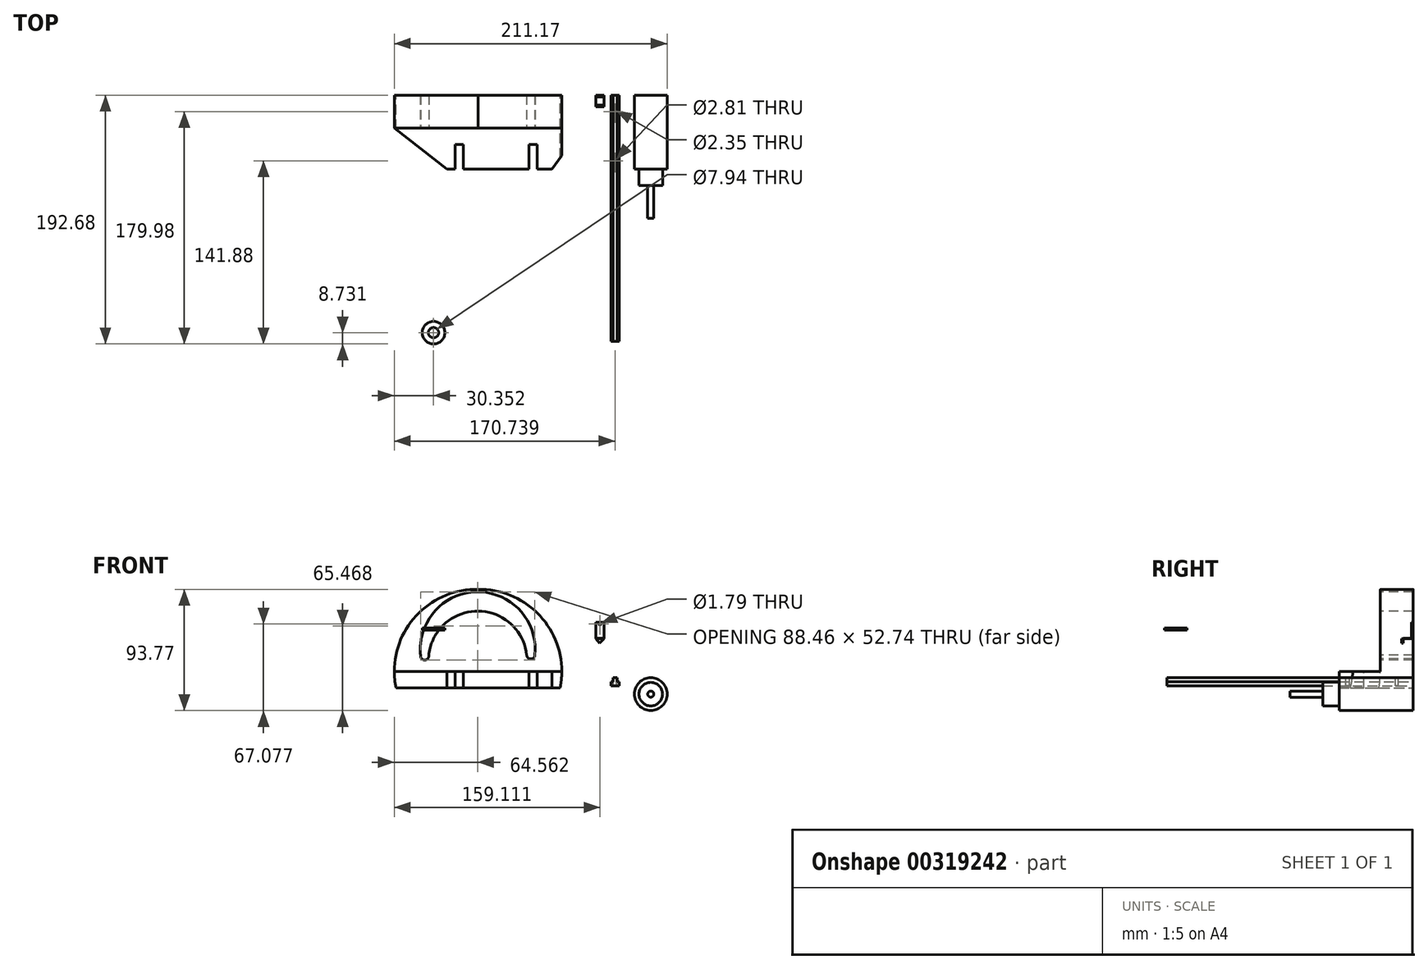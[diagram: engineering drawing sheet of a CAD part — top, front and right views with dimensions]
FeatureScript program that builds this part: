
annotation { "Feature Type Name" : "Feature", "Feature Type Description" : "" }
export const myFeature = defineFeature(function(context is Context, id is Id, definition is map)
    precondition{}
    {
        {
            var Q0;
            Q0=qCreatedBy(makeId("Front.planeOp"),FACE);
            var sketch = newSketch(context, id + "F0", { "sketchPlane" : qUnion([Q0])});
            skLineSegment(sketch, "E0", {"start": v(-59.8, -44.8) * mm, "end": v(67.2, -44.8) * mm});
            skLineSegment(sketch, "E1", {"start": v(-59.8, -44.8) * mm, "end": v(3.7, -44.8) * mm});
            skLineSegment(sketch, "E2", {"start": v(3.7, -44.8) * mm, "end": v(3.7, 31.4) * mm});
            skArc(sketch, "E3", {"start": v(67.2, -44.8) * mm, "mid": v(53.77, 8.57) * mm, "end": v(3.7, 31.4) * mm});
            skArc(sketch, "E4", {"start": v(3.7, 31.4) * mm, "mid": v(-46.37, 8.57) * mm, "end": v(-59.8, -44.8) * mm});
            skSolve(sketch);
        }
        {
            var Q0;
            Q0=makeQuery(id+"F0.imprint","IMPRINT",FACE,{"disambiguationData":[TD([[makeQuery(id+"F0.imprint","IMPRINT",EDGE,{"derivedFrom":sQuery(id+"F0.wireOp",EDGE,"E1")}),1.0]])]});
            var Q1;
            Q1=makeQuery(id+"F0.imprint","IMPRINT",FACE,{"disambiguationData":[TD([[makeQuery(id+"F0.imprint","IMPRINT",EDGE,{"derivedFrom":sQuery(id+"F0.wireOp",EDGE,"E0")}),1.0]])]});
            extrude(context, id + "F1", {"entities" : qUnion([Q0, Q1]), "depth" : 25.4 * mm});
        }
        {
            var Q0;
            Q0=makeQuery(id+"F1.opExtrude","CAP_FACE",FACE,{"disambiguationData":[OSD([sQuery(id+"F0.wireOp",EDGE,"E0"),sQuery(id+"F0.wireOp",EDGE,"E1"),sQuery(id+"F0.wireOp",EDGE,"E3"),sQuery(id+"F0.wireOp",EDGE,"E4")])],"isStart":false});
            var sketch = newSketch(context, id + "F2", { "sketchPlane" : qUnion([Q0])});
            skLineSegment(sketch, "E5", {"start": v(3.7, -44.8) * mm, "end": v(3.7, -32.1) * mm});
            skLineSegment(sketch, "E6", {"start": v(3.7, -32.1) * mm, "end": v(68.48, -32.1) * mm});
            skLineSegment(sketch, "E7", {"start": v(68.48, -32.1) * mm, "end": v(-61.09, -32.1) * mm});
            skSolve(sketch);
        }
        {
            var Q0;
            Q0 = qSketchRegion(id + "F2", true);
            var Q1;
            {var subQ0=sQuery(id+"F2.wireOp",EDGE,"E5");Q1=makeQuery(id+"F2.imprint","IMPRINT",FACE,{"disambiguationData":[TD([[makeQuery(id+"F2.imprint","IMPRINT",EDGE,{"derivedFrom":subQ0}),-1.0]])]});}
            var Q2;
            {var subQ0=sQuery(id+"F2.wireOp",EDGE,"E5");Q2=makeQuery(id+"F2.imprint","IMPRINT",FACE,{"disambiguationData":[TD([[makeQuery(id+"F2.imprint","IMPRINT",EDGE,{"derivedFrom":subQ0}),1.0]])]});}
            extrude(context, id + "F3", {"entities" : qUnion([Q0, Q1, Q2]), "operationType" : NewBodyOperationType.ADD, "depth" : 31.75 * mm});
        }
        {
            var Q0;
            Q0=makeQuery(id+"F3.opExtrude","SWEPT_FACE",FACE,{"disambiguationData":[OSD([sQuery(id+"F2.wireOp",EDGE,"E7")])]});
            var sketch = newSketch(context, id + "F4", { "sketchPlane" : qUnion([Q0])});
            skLineSegment(sketch, "E8", {"start": v(68.48, -57.15) * mm, "end": v(-20.42, -57.15) * mm});
            skLineSegment(sketch, "E9", {"start": v(-20.42, -57.15) * mm, "end": v(-61.09, -25.4) * mm});
            skLineSegment(sketch, "E10", {"start": v(-20.42, -57.15) * mm, "end": v(-14.07, -57.15) * mm});
            skLineSegment(sketch, "E11", {"start": v(-14.07, -57.15) * mm, "end": v(-14.07, -38.1) * mm});
            skLineSegment(sketch, "E12", {"start": v(-14.07, -38.1) * mm, "end": v(-7.72, -38.1) * mm});
            skLineSegment(sketch, "E13", {"start": v(-7.72, -38.1) * mm, "end": v(-7.72, -57.15) * mm});
            skLineSegment(sketch, "E14", {"start": v(-7.72, -57.15) * mm, "end": v(43.08, -57.15) * mm});
            skLineSegment(sketch, "E15", {"start": v(43.08, -57.15) * mm, "end": v(43.08, -38.1) * mm});
            skLineSegment(sketch, "E16", {"start": v(43.08, -38.1) * mm, "end": v(49.43, -38.1) * mm});
            skLineSegment(sketch, "E17", {"start": v(49.43, -38.1) * mm, "end": v(49.43, -57.15) * mm});
            skSolve(sketch);
        }
        {
            var Q0;
            {var subQ0=sQuery(id+"F4.wireOp",EDGE,"E11");Q0=makeQuery(id+"F4.imprint","IMPRINT",FACE,{"disambiguationData":[TD([[makeQuery(id+"F4.imprint","IMPRINT",EDGE,{"derivedFrom":subQ0}),-1.0]])]});}
            var Q1;
            {var subQ0=sQuery(id+"F4.wireOp",EDGE,"E15");Q1=makeQuery(id+"F4.imprint","IMPRINT",FACE,{"disambiguationData":[TD([[makeQuery(id+"F4.imprint","IMPRINT",EDGE,{"derivedFrom":subQ0}),-1.0]])]});}
            extrude(context, id + "F5", {"entities" : qUnion([Q0, Q1]), "operationType" : NewBodyOperationType.REMOVE, "oppositeDirection" : true, "depth" : 25.4 * mm});
        }
        {
            var Q0;
            Q0=makeQuery(id+"F3.opExtrude","SWEPT_FACE",FACE,{"disambiguationData":[OSD([sQuery(id+"F2.wireOp",EDGE,"E7")])]});
            var sketch = newSketch(context, id + "F6", { "sketchPlane" : qUnion([Q0])});
            skLineSegment(sketch, "E18", {"start": v(-14.07, -57.15) * mm, "end": v(-20.42, -57.15) * mm});
            skLineSegment(sketch, "E19", {"start": v(-20.42, -57.15) * mm, "end": v(-61.09, -25.48) * mm});
            skSolve(sketch);
        }
        {
            var Q0;
            Q0 = qSketchRegion(id + "F6", true);
            var Q1;
            {var subQ0=sQuery(id+"F6.wireOp",EDGE,"E19");Q1=makeQuery(id+"F6.imprint","IMPRINT",FACE,{"disambiguationData":[TD([[makeQuery(id+"F6.imprint","IMPRINT",EDGE,{"derivedFrom":subQ0}),1.0]])]});}
            extrude(context, id + "F7", {"entities" : qUnion([Q0, Q1]), "operationType" : NewBodyOperationType.REMOVE, "oppositeDirection" : true, "depth" : 25.4 * mm});
        }
        {
            var Q0;
            Q0=qCreatedBy(makeId("Front.planeOp"),FACE);
            var sketch = newSketch(context, id + "F8", { "sketchPlane" : qUnion([Q0])});
            skLineSegment(sketch, "E20", {"start": v(106.47, -43.18) * mm, "end": v(112.82, -43.18) * mm});
            skLineSegment(sketch, "E21", {"start": v(112.82, -43.18) * mm, "end": v(112.82, -40) * mm});
            skLineSegment(sketch, "E22", {"start": v(112.82, -40) * mm, "end": v(111.24, -40) * mm});
            skLineSegment(sketch, "E23", {"start": v(111.24, -40) * mm, "end": v(111.24, -36.83) * mm});
            skLineSegment(sketch, "E24", {"start": v(106.47, -43.18) * mm, "end": v(106.47, -40) * mm});
            skLineSegment(sketch, "E25", {"start": v(106.47, -40) * mm, "end": v(108.06, -40) * mm});
            skLineSegment(sketch, "E26", {"start": v(108.06, -40) * mm, "end": v(108.06, -36.83) * mm});
            skLineSegment(sketch, "E27", {"start": v(108.06, -36.83) * mm, "end": v(111.24, -36.83) * mm});
            skSolve(sketch);
        }
        {
            var Q0;
            Q0 = qSketchRegion(id + "F8", true);
            var Q1;
            Q1=makeQuery(id+"F8.imprint","IMPRINT",FACE,{"disambiguationData":[TD([[makeQuery(id+"F8.imprint","IMPRINT",EDGE,{"derivedFrom":sQuery(id+"F8.wireOp",EDGE,"E20")}),1.0]])]});
            extrude(context, id + "F9", {"entities" : qUnion([Q0, Q1]), "depth" : 190.5 * mm});
        }
        {
            var Q0;
            Q0=makeQuery(id+"F1.opExtrude","CAP_FACE",FACE,{"disambiguationData":[OSD([sQuery(id+"F0.wireOp",EDGE,"E0"),sQuery(id+"F0.wireOp",EDGE,"E1"),sQuery(id+"F0.wireOp",EDGE,"E3"),sQuery(id+"F0.wireOp",EDGE,"E4")])],"isStart":false});
            var sketch = newSketch(context, id + "F10", { "sketchPlane" : qUnion([Q0])});
            skArc(sketch, "E28", {"start": v(41.35, -19.4) * mm, "mid": v(3.47, 14.6) * mm, "end": v(-34.4, -19.4) * mm});
            skArc(sketch, "E29", {"start": v(47.7, -19.4) * mm, "mid": v(3.47, 29.5) * mm, "end": v(-40.76, -19.4) * mm});
            skPoint(sketch, "E30.end.orphan", {"position": v(-34.4, -32.1) * mm});
            skPoint(sketch, "E31.end.orphan", {"position": v(41.35, -32.1) * mm});
            skArc(sketch, "E32", {"start": v(-40.76, -19.4) * mm, "mid": v(-37.58, -23.25) * mm, "end": v(-34.4, -19.4) * mm});
            skArc(sketch, "E33", {"start": v(41.35, -19.4) * mm, "mid": v(44.53, -22.45) * mm, "end": v(47.7, -19.4) * mm});
            skSolve(sketch);
        }
        {
            var Q0;
            Q0=makeQuery(id+"F10.imprint","IMPRINT",FACE,{"disambiguationData":[TD([[makeQuery(id+"F10.imprint","IMPRINT",EDGE,{"derivedFrom":sQuery(id+"F10.wireOp",EDGE,"E28")}),-1.0]])]});
            extrude(context, id + "F11", {"entities" : qUnion([Q0]), "operationType" : NewBodyOperationType.REMOVE, "oppositeDirection" : true, "depth" : 25.4 * mm});
        }
        {
            var Q0;
            Q0=makeQuery(id+"F3.opExtrude","SWEPT_FACE",FACE,{"disambiguationData":[OSD([sQuery(id+"F2.wireOp",EDGE,"E7")])]});
            var sketch = newSketch(context, id + "F12", { "sketchPlane" : qUnion([Q0])});
            skLineSegment(sketch, "E34", {"start": v(61, -57.15) * mm, "end": v(68.48, -46.88) * mm});
            skSolve(sketch);
        }
        {
            var Q0;
            Q0 = qSketchRegion(id + "F12", true);
            var Q1;
            {var subQ0=sQuery(id+"F12.wireOp",EDGE,"E34");Q1=makeQuery(id+"F12.imprint","IMPRINT",FACE,{"disambiguationData":[TD([[makeQuery(id+"F12.imprint","IMPRINT",EDGE,{"derivedFrom":subQ0}),-1.0]])]});}
            extrude(context, id + "F13", {"entities" : qUnion([Q0, Q1]), "operationType" : NewBodyOperationType.REMOVE, "oppositeDirection" : true, "depth" : 25.4 * mm});
        }
        {
            var Q0;
            Q0=qCreatedBy(makeId("Front.planeOp"),FACE);
            var sketch = newSketch(context, id + "F14", { "sketchPlane" : qUnion([Q0])});
            skCircle(sketch, "E35", {"center": v(137.38, -49.65) * mm, "radius": 12.7 * mm});
            skSolve(sketch);
        }
        {
            var Q0;
            Q0 = qSketchRegion(id + "F14", true);
            var Q1;
            Q1=makeQuery(id+"F14.imprint","IMPRINT",FACE,{"disambiguationData":[TD([[makeQuery(id+"F14.imprint","IMPRINT",EDGE,{"derivedFrom":sQuery(id+"F14.wireOp",EDGE,"E35")}),1.0]])]});
            extrude(context, id + "F15", {"entities" : qUnion([Q0, Q1]), "depth" : 57.15 * mm});
        }
        {
            var Q0;
            Q0=makeQuery(id+"F15.opExtrude","CAP_FACE",FACE,{"disambiguationData":[OSD([sQuery(id+"F14.wireOp",EDGE,"E35")])],"isStart":false});
            var sketch = newSketch(context, id + "F16", { "sketchPlane" : qUnion([Q0])});
            skCircle(sketch, "E36", {"center": v(137.38, -49.65) * mm, "radius": 9.13 * mm});
            skSolve(sketch);
        }
        {
            var Q0;
            Q0=makeQuery(id+"F16.imprint","IMPRINT",FACE,{"disambiguationData":[TD([[makeQuery(id+"F16.imprint","IMPRINT",EDGE,{"derivedFrom":sQuery(id+"F16.wireOp",EDGE,"E36")}),1.0]])]});
            extrude(context, id + "F17", {"entities" : qUnion([Q0]), "operationType" : NewBodyOperationType.ADD, "depth" : 12.7 * mm});
        }
        {
            var Q0;
            Q0=makeQuery(id+"F17.opExtrude","CAP_FACE",FACE,{"disambiguationData":[OSD([sQuery(id+"F16.wireOp",EDGE,"E36")])],"isStart":false});
            var sketch = newSketch(context, id + "F18", { "sketchPlane" : qUnion([Q0])});
            skCircle(sketch, "E37", {"center": v(137.38, -49.65) * mm, "radius": 2.38 * mm});
            skSolve(sketch);
        }
        {
            var Q0;
            Q0=makeQuery(id+"F18.imprint","IMPRINT",FACE,{"disambiguationData":[TD([[makeQuery(id+"F18.imprint","IMPRINT",EDGE,{"derivedFrom":sQuery(id+"F18.wireOp",EDGE,"E37")}),1.0]])]});
            extrude(context, id + "F19", {"entities" : qUnion([Q0]), "operationType" : NewBodyOperationType.ADD, "depth" : 25.4 * mm});
        }
        {
            var Q0;
            Q0=makeQuery(id+"F9.opExtrude","SWEPT_FACE",FACE,{"disambiguationData":[OSD([sQuery(id+"F8.wireOp",EDGE,"E27")])]});
            var sketch = newSketch(context, id + "F20", { "sketchPlane" : qUnion([Q0])});
            skLineSegment(sketch, "E38", {"start": v(109.65, -190.5) * mm, "end": v(109.65, -50.8) * mm});
            skCircle(sketch, "E39", {"center": v(109.65, -50.8) * mm, "radius": 1.4 * mm});
            skSolve(sketch);
        }
        {
            var Q0;
            Q0=makeQuery(id+"F20.imprint","IMPRINT",FACE,{"disambiguationData":[TD([[makeQuery(id+"F20.imprint","IMPRINT",EDGE,{"derivedFrom":sQuery(id+"F20.wireOp",EDGE,"E39")}),1.0]])]});
            extrude(context, id + "F21", {"entities" : qUnion([Q0]), "operationType" : NewBodyOperationType.REMOVE, "oppositeDirection" : true, "depth" : 25.4 * mm});
        }
        {
            var Q0;
            Q0=qCreatedBy(makeId("Top.planeOp"),FACE);
            var sketch = newSketch(context, id + "F22", { "sketchPlane" : qUnion([Q0])});
            skCircle(sketch, "E40", {"center": v(-30.74, -183.95) * mm, "radius": 8.73 * mm});
            skCircle(sketch, "E41", {"center": v(-30.74, -183.95) * mm, "radius": 3.97 * mm});
            skSolve(sketch);
        }
        {
            var Q0;
            Q0=makeQuery(id+"F22.imprint","IMPRINT",FACE,{"disambiguationData":[TD([[makeQuery(id+"F22.imprint","IMPRINT",EDGE,{"derivedFrom":sQuery(id+"F22.wireOp",EDGE,"E40")}),1.0]])]});
            extrude(context, id + "F23", {"entities" : qUnion([Q0]), "depth" : 1.59 * mm});
        }
        {
            var Q0;
            Q0=qCreatedBy(makeId("Front.planeOp"),FACE);
            var sketch = newSketch(context, id + "F24", { "sketchPlane" : qUnion([Q0])});
            skLineSegment(sketch, "E42", {"start": v(94.85, 6) * mm, "end": v(94.85, -6.7) * mm});
            skLineSegment(sketch, "E43", {"start": v(94.85, -6.7) * mm, "end": v(101.2, -6.7) * mm});
            skLineSegment(sketch, "E44", {"start": v(101.2, -6.7) * mm, "end": v(101.2, 6) * mm});
            skLineSegment(sketch, "E45", {"start": v(101.2, 6) * mm, "end": v(94.85, 6) * mm});
            skSolve(sketch);
        }
        {
            var Q0;
            Q0 = qSketchRegion(id + "F24", true);
            var Q1;
            Q1=makeQuery(id+"F24.imprint","IMPRINT",FACE,{"disambiguationData":[TD([[makeQuery(id+"F24.imprint","IMPRINT",EDGE,{"derivedFrom":sQuery(id+"F24.wireOp",EDGE,"E42")}),1.0]])]});
            extrude(context, id + "F25", {"entities" : qUnion([Q0, Q1]), "depth" : 1.41 * mm});
        }
        {
            var Q0;
            Q0=makeQuery(id+"F25.opExtrude","CAP_FACE",FACE,{"disambiguationData":[OSD([sQuery(id+"F24.wireOp",EDGE,"E42"),sQuery(id+"F24.wireOp",EDGE,"E43"),sQuery(id+"F24.wireOp",EDGE,"E44"),sQuery(id+"F24.wireOp",EDGE,"E45")])],"isStart":false});
            var sketch = newSketch(context, id + "F26", { "sketchPlane" : qUnion([Q0])});
            skLineSegment(sketch, "E46", {"start": v(94.85, -6.37) * mm, "end": v(101.2, -6.37) * mm});
            skLineSegment(sketch, "E47", {"start": v(101.2, -6.37) * mm, "end": v(101.2, -6.7) * mm});
            skLineSegment(sketch, "E48", {"start": v(101.2, -6.7) * mm, "end": v(94.85, -6.7) * mm});
            skLineSegment(sketch, "E49", {"start": v(94.85, -6.7) * mm, "end": v(94.85, -6.37) * mm});
            skSolve(sketch);
        }
        {
            var Q0;
            Q0=makeQuery(id+"F26.imprint","IMPRINT",FACE,{"disambiguationData":[TD([[makeQuery(id+"F26.imprint","IMPRINT",EDGE,{"derivedFrom":sQuery(id+"F26.wireOp",EDGE,"E46")}),-1.0]])]});
            extrude(context, id + "F27", {"entities" : qUnion([Q0]), "operationType" : NewBodyOperationType.ADD, "depth" : 6.35 * mm});
        }
        {
            var Q0;
            Q0=makeQuery(id+"F27.opExtrude","CAP_FACE",FACE,{"disambiguationData":[OSD([sQuery(id+"F26.wireOp",EDGE,"E46"),sQuery(id+"F26.wireOp",EDGE,"E47"),sQuery(id+"F26.wireOp",EDGE,"E48"),sQuery(id+"F26.wireOp",EDGE,"E49")])],"isStart":false});
            var sketch = newSketch(context, id + "F28", { "sketchPlane" : qUnion([Q0])});
            skLineSegment(sketch, "E50", {"start": v(94.85, -6.7) * mm, "end": v(97.84, -10.12) * mm});
            skLineSegment(sketch, "E51", {"start": v(97.84, -10.12) * mm, "end": v(101.2, -6.7) * mm});
            skSolve(sketch);
        }
        {
            var Q0;
            Q0 = qSketchRegion(id + "F28", true);
            var Q1;
            Q1=makeQuery(id+"F28.imprint","IMPRINT",FACE,{"disambiguationData":[TD([[makeQuery(id+"F28.imprint","IMPRINT",EDGE,{"derivedFrom":sQuery(id+"F28.wireOp",EDGE,"E50")}),1.0]])]});
            extrude(context, id + "F29", {"entities" : qUnion([Q0, Q1]), "depth" : 1.41 * mm});
        }
        {
            var Q0;
            Q0=makeQuery(id+"F25.opExtrude","CAP_FACE",FACE,{"disambiguationData":[OSD([sQuery(id+"F24.wireOp",EDGE,"E42"),sQuery(id+"F24.wireOp",EDGE,"E43"),sQuery(id+"F24.wireOp",EDGE,"E44"),sQuery(id+"F24.wireOp",EDGE,"E45")])],"isStart":false});
            var sketch = newSketch(context, id + "F30", { "sketchPlane" : qUnion([Q0])});
            skLineSegment(sketch, "E52", {"start": v(98.02, 6) * mm, "end": v(98.02, 4.73) * mm});
            skPoint(sketch, "E52.endSnap0", {"position": v(98.02, 6) * mm});
            skCircle(sketch, "E53", {"center": v(98.02, 4.73) * mm, "radius": 0.9 * mm});
            skSolve(sketch);
        }
        {
            var Q0;
            Q0=makeQuery(id+"F30.imprint","IMPRINT",FACE,{"disambiguationData":[TD([[makeQuery(id+"F30.imprint","IMPRINT",EDGE,{"derivedFrom":sQuery(id+"F30.wireOp",EDGE,"E53")}),1.0]])]});
            extrude(context, id + "F31", {"entities" : qUnion([Q0]), "operationType" : NewBodyOperationType.REMOVE, "oppositeDirection" : true, "depth" : 25.4 * mm});
        }
        {
            var Q0;
            Q0=makeQuery(id+"F9.opExtrude","SWEPT_FACE",FACE,{"disambiguationData":[OSD([sQuery(id+"F8.wireOp",EDGE,"E27")])]});
            var sketch = newSketch(context, id + "F32", { "sketchPlane" : qUnion([Q0])});
            skLineSegment(sketch, "E54", {"start": v(109.65, 0) * mm, "end": v(109.65, -12.7) * mm});
            skCircle(sketch, "E55", {"center": v(109.65, -12.7) * mm, "radius": 1.18 * mm});
            skSolve(sketch);
        }
        {
            var Q0;
            Q0=makeQuery(id+"F32.imprint","IMPRINT",FACE,{"disambiguationData":[TD([[makeQuery(id+"F32.imprint","IMPRINT",EDGE,{"derivedFrom":sQuery(id+"F32.wireOp",EDGE,"E55")}),1.0]])]});
            extrude(context, id + "F33", {"entities" : qUnion([Q0]), "operationType" : NewBodyOperationType.REMOVE, "oppositeDirection" : true, "depth" : 25.4 * mm});
        }
    });
